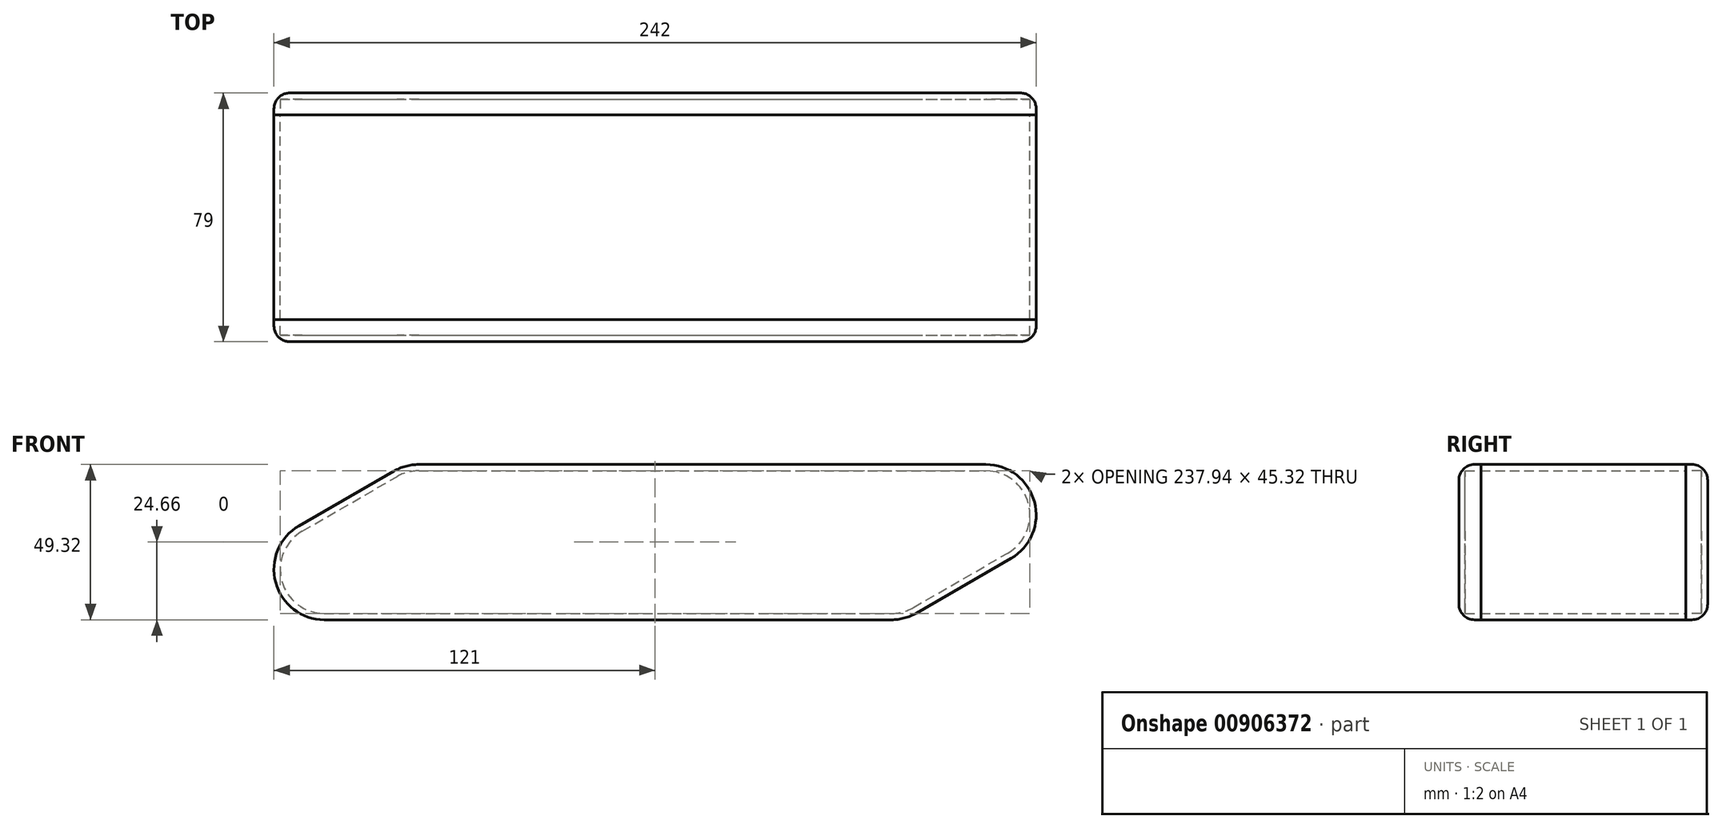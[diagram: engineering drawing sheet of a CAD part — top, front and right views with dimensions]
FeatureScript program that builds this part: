
annotation { "Feature Type Name" : "Feature", "Feature Type Description" : "" }
export const myFeature = defineFeature(function(context is Context, id is Id, definition is map)
    precondition{}
    {
        {
            var Q0;
            Q0=qCreatedBy(makeId("Front.planeOp"),FACE);
            var sketch = newSketch(context, id + "F0", { "sketchPlane" : qUnion([Q0])});
            skCircle(sketch, "E0", {"center": v(0, 0) * mm, "radius": 9 * mm});
            skCircle(sketch, "E1.1.0.0", {"center": v(20, 0) * mm, "radius": 9 * mm});
            skCircle(sketch, "E1.2.0.0", {"center": v(40, 0) * mm, "radius": 9 * mm});
            skCircle(sketch, "E1.3.0.0", {"center": v(60, 0) * mm, "radius": 9 * mm});
            skCircle(sketch, "E1.4.0.0", {"center": v(80, 0) * mm, "radius": 9 * mm});
            skCircle(sketch, "E1.5.0.0", {"center": v(100, 0) * mm, "radius": 9 * mm});
            skCircle(sketch, "E1.6.0.0", {"center": v(120, 0) * mm, "radius": 9 * mm});
            skCircle(sketch, "E1.7.0.0", {"center": v(140, 0) * mm, "radius": 9 * mm});
            skCircle(sketch, "E1.8.0.0", {"center": v(160, 0) * mm, "radius": 9 * mm});
            skCircle(sketch, "E1.9.0.0", {"center": v(180, 0) * mm, "radius": 9 * mm});
            skLineSegment(sketch, "E1.direction1", {"start": v(0, 0) * mm, "end": v(20, 0) * mm, "construction": true});
            skCircle(sketch, "E2", {"center": v(30, 17.32) * mm, "radius": 9 * mm});
            skCircle(sketch, "E3.1.0.0", {"center": v(50, 17.32) * mm, "radius": 9 * mm});
            skCircle(sketch, "E3.2.0.0", {"center": v(70, 17.32) * mm, "radius": 9 * mm});
            skCircle(sketch, "E3.3.0.0", {"center": v(90, 17.32) * mm, "radius": 9 * mm});
            skCircle(sketch, "E3.4.0.0", {"center": v(110, 17.32) * mm, "radius": 9 * mm});
            skCircle(sketch, "E3.5.0.0", {"center": v(130, 17.32) * mm, "radius": 9 * mm});
            skCircle(sketch, "E3.6.0.0", {"center": v(150, 17.32) * mm, "radius": 9 * mm});
            skCircle(sketch, "E3.7.0.0", {"center": v(170, 17.32) * mm, "radius": 9 * mm});
            skCircle(sketch, "E3.8.0.0", {"center": v(190, 17.32) * mm, "radius": 9 * mm});
            skCircle(sketch, "E3.9.0.0", {"center": v(210, 17.32) * mm, "radius": 9 * mm});
            skLineSegment(sketch, "E3.direction1", {"start": v(30, 17.32) * mm, "end": v(50, 17.32) * mm, "construction": true});
            skSolve(sketch);
        }
        {
            var Q0;
            Q0=qCreatedBy(makeId("Front.planeOp"),FACE);
            var sketch = newSketch(context, id + "F1", { "sketchPlane" : qUnion([Q0])});
            skArc(sketch, "E4.0", {"start": v(-4.5, 7.8) * mm, "mid": v(-8.7, -2.33) * mm, "end": v(0, -9) * mm});
            skArc(sketch, "E5.0", {"start": v(30, 26.32) * mm, "mid": v(27.67, 26.01) * mm, "end": v(25.5, 25.11) * mm});
            skArc(sketch, "E6.0", {"start": v(214.5, 9.53) * mm, "mid": v(218.7, 19.65) * mm, "end": v(210, 26.32) * mm});
            skArc(sketch, "E7.0", {"start": v(180, -9) * mm, "mid": v(182.33, -8.7) * mm, "end": v(184.5, -7.8) * mm});
            skLineSegment(sketch, "E8", {"start": v(-4.5, 7.8) * mm, "end": v(25.5, 25.11) * mm});
            skLineSegment(sketch, "E9", {"start": v(0, -9) * mm, "end": v(180, -9) * mm});
            skLineSegment(sketch, "E10", {"start": v(184.5, -7.8) * mm, "end": v(214.5, 9.53) * mm});
            skLineSegment(sketch, "E11", {"start": v(30, 26.32) * mm, "end": v(210, 26.32) * mm});
            skArc(sketch, "E12.0", {"start": v(30, 31.32) * mm, "mid": v(26.38, 30.84) * mm, "end": v(23, 29.44) * mm});
            skLineSegment(sketch, "E12.1", {"start": v(-7, 12.12) * mm, "end": v(23, 29.44) * mm});
            skLineSegment(sketch, "E12.2", {"start": v(30, 31.32) * mm, "end": v(210, 31.32) * mm});
            skArc(sketch, "E12.3", {"start": v(-7, 12.12) * mm, "mid": v(-13.52, -3.62) * mm, "end": v(0, -14) * mm});
            skArc(sketch, "E12.4", {"start": v(217, 5.2) * mm, "mid": v(223.52, 20.94) * mm, "end": v(210, 31.32) * mm});
            skLineSegment(sketch, "E12.5", {"start": v(187, -12.12) * mm, "end": v(217, 5.2) * mm});
            skArc(sketch, "E12.6", {"start": v(180, -14) * mm, "mid": v(183.62, -13.52) * mm, "end": v(187, -12.12) * mm});
            skLineSegment(sketch, "E12.7", {"start": v(0, -14) * mm, "end": v(180, -14) * mm});
            skArc(sketch, "E13.0", {"start": v(30, 33.32) * mm, "mid": v(25.86, 32.78) * mm, "end": v(22, 31.18) * mm});
            skLineSegment(sketch, "E13.1", {"start": v(-8, 13.86) * mm, "end": v(22, 31.18) * mm});
            skLineSegment(sketch, "E13.2", {"start": v(30, 33.32) * mm, "end": v(210, 33.32) * mm});
            skArc(sketch, "E13.3", {"start": v(-8, 13.86) * mm, "mid": v(-15.45, -4.14) * mm, "end": v(0, -16) * mm});
            skArc(sketch, "E13.4", {"start": v(218, 3.46) * mm, "mid": v(225.45, 21.46) * mm, "end": v(210, 33.32) * mm});
            skLineSegment(sketch, "E13.5", {"start": v(188, -13.86) * mm, "end": v(218, 3.46) * mm});
            skArc(sketch, "E13.6", {"start": v(180, -16) * mm, "mid": v(184.14, -15.45) * mm, "end": v(188, -13.86) * mm});
            skLineSegment(sketch, "E13.7", {"start": v(0, -16) * mm, "end": v(180, -16) * mm});
            skSolve(sketch);
        }
        {
            var Q0;
            Q0=makeQuery(id+"F1.imprint","IMPRINT",FACE,{"disambiguationData":[TD([[makeQuery(id+"F1.imprint","IMPRINT",EDGE,{"derivedFrom":sQuery(id+"F1.wireOp",EDGE,"E12.0")}),-1.0]])]});
            extrude(context, id + "F2", {"entities" : qUnion([Q0]), "depth" : 65 * mm, "offsetDistance" : 25 * mm});
        }
        {
            var Q0;
            Q0=makeQuery(id+"F2.opExtrude","CAP_FACE",FACE,{"disambiguationData":[OSD([sQuery(id+"F1.wireOp",EDGE,"E12.0"),sQuery(id+"F1.wireOp",EDGE,"E12.1"),sQuery(id+"F1.wireOp",EDGE,"E12.2"),sQuery(id+"F1.wireOp",EDGE,"E12.3"),sQuery(id+"F1.wireOp",EDGE,"E12.4"),sQuery(id+"F1.wireOp",EDGE,"E12.5"),sQuery(id+"F1.wireOp",EDGE,"E12.6"),sQuery(id+"F1.wireOp",EDGE,"E12.7"),sQuery(id+"F1.wireOp",EDGE,"E13.0"),sQuery(id+"F1.wireOp",EDGE,"E13.1"),sQuery(id+"F1.wireOp",EDGE,"E13.2"),sQuery(id+"F1.wireOp",EDGE,"E13.3"),sQuery(id+"F1.wireOp",EDGE,"E13.4"),sQuery(id+"F1.wireOp",EDGE,"E13.5"),sQuery(id+"F1.wireOp",EDGE,"E13.6"),sQuery(id+"F1.wireOp",EDGE,"E13.7")])],"isStart":false});
            var sketch = newSketch(context, id + "F3", { "sketchPlane" : qUnion([Q0])});
            skArc(sketch, "E14.0.0", {"start": v(-8, 13.86) * mm, "mid": v(-15.45, -4.14) * mm, "end": v(0, -16) * mm});
            skLineSegment(sketch, "E14.0.1", {"start": v(0, -16) * mm, "end": v(180, -16) * mm});
            skArc(sketch, "E14.0.2", {"start": v(180, -16) * mm, "mid": v(184.14, -15.45) * mm, "end": v(188, -13.86) * mm});
            skLineSegment(sketch, "E14.0.3", {"start": v(188, -13.86) * mm, "end": v(218, 3.46) * mm});
            skArc(sketch, "E14.0.4", {"start": v(218, 3.46) * mm, "mid": v(225.45, 21.46) * mm, "end": v(210, 33.32) * mm});
            skLineSegment(sketch, "E14.0.5", {"start": v(210, 33.32) * mm, "end": v(30, 33.32) * mm});
            skArc(sketch, "E14.0.6", {"start": v(30, 33.32) * mm, "mid": v(25.86, 32.78) * mm, "end": v(22, 31.18) * mm});
            skLineSegment(sketch, "E14.0.7", {"start": v(22, 31.18) * mm, "end": v(-8, 13.86) * mm});
            skLineSegment(sketch, "E15.0", {"start": v(30, 31.32) * mm, "end": v(210, 31.32) * mm});
            skArc(sketch, "E16.0", {"start": v(30, 31.32) * mm, "mid": v(26.38, 30.84) * mm, "end": v(23, 29.44) * mm});
            skLineSegment(sketch, "E17.0", {"start": v(-7, 12.12) * mm, "end": v(23, 29.44) * mm});
            skArc(sketch, "E18.0", {"start": v(-7, 12.12) * mm, "mid": v(-13.52, -3.62) * mm, "end": v(0, -14) * mm});
            skLineSegment(sketch, "E19.0", {"start": v(0, -14) * mm, "end": v(180, -14) * mm});
            skArc(sketch, "E20.0", {"start": v(180, -14) * mm, "mid": v(183.62, -13.52) * mm, "end": v(187, -12.12) * mm});
            skLineSegment(sketch, "E21.0", {"start": v(187, -12.12) * mm, "end": v(217, 5.2) * mm});
            skArc(sketch, "E22.0", {"start": v(217, 5.2) * mm, "mid": v(223.52, 20.94) * mm, "end": v(210, 31.32) * mm});
            skSolve(sketch);
        }
        {
            var Q0;
            Q0=makeQuery(id+"F3.imprint","IMPRINT",FACE,{"disambiguationData":[TD([[makeQuery(id+"F3.imprint","IMPRINT",EDGE,{"derivedFrom":sQuery(id+"F3.wireOp",EDGE,"E14.0.0")}),1.0]])]});
            extrude(context, id + "F4", {"entities" : qUnion([Q0]), "depth" : 5 * mm, "offsetDistance" : 25 * mm});
        }
        {
            var Q0;
            Q0=makeQuery(id+"F4.opExtrude","CAP_FACE",FACE,{"disambiguationData":[OSD([sQuery(id+"F3.wireOp",EDGE,"E14.0.0"),sQuery(id+"F3.wireOp",EDGE,"E14.0.1"),sQuery(id+"F3.wireOp",EDGE,"E14.0.2"),sQuery(id+"F3.wireOp",EDGE,"E14.0.3"),sQuery(id+"F3.wireOp",EDGE,"E14.0.4"),sQuery(id+"F3.wireOp",EDGE,"E14.0.5"),sQuery(id+"F3.wireOp",EDGE,"E14.0.6"),sQuery(id+"F3.wireOp",EDGE,"E14.0.7"),sQuery(id+"F3.wireOp",EDGE,"E15.0"),sQuery(id+"F3.wireOp",EDGE,"E16.0"),sQuery(id+"F3.wireOp",EDGE,"E17.0"),sQuery(id+"F3.wireOp",EDGE,"E18.0"),sQuery(id+"F3.wireOp",EDGE,"E19.0"),sQuery(id+"F3.wireOp",EDGE,"E20.0"),sQuery(id+"F3.wireOp",EDGE,"E21.0"),sQuery(id+"F3.wireOp",EDGE,"E22.0")])],"isStart":false});
            var sketch = newSketch(context, id + "F5", { "sketchPlane" : qUnion([Q0])});
            skLineSegment(sketch, "E23.0.0", {"start": v(22, 31.18) * mm, "end": v(-8, 13.86) * mm});
            skArc(sketch, "E23.0.1", {"start": v(-8, 13.86) * mm, "mid": v(-15.45, -4.14) * mm, "end": v(0, -16) * mm});
            skLineSegment(sketch, "E23.0.2", {"start": v(0, -16) * mm, "end": v(180, -16) * mm});
            skArc(sketch, "E23.0.3", {"start": v(180, -16) * mm, "mid": v(184.14, -15.45) * mm, "end": v(188, -13.86) * mm});
            skLineSegment(sketch, "E23.0.4", {"start": v(188, -13.86) * mm, "end": v(218, 3.46) * mm});
            skArc(sketch, "E23.0.5", {"start": v(218, 3.46) * mm, "mid": v(225.45, 21.46) * mm, "end": v(210, 33.32) * mm});
            skLineSegment(sketch, "E23.0.6", {"start": v(210, 33.32) * mm, "end": v(30, 33.32) * mm});
            skArc(sketch, "E23.0.7", {"start": v(30, 33.32) * mm, "mid": v(25.86, 32.78) * mm, "end": v(22, 31.18) * mm});
            skSolve(sketch);
        }
        {
            var Q0;
            Q0=makeQuery(id+"F5.imprint","IMPRINT",FACE,{"disambiguationData":[TD([[makeQuery(id+"F5.imprint","IMPRINT",EDGE,{"derivedFrom":makeQuery(id+"F4.opExtrude","CAP_EDGE",EDGE,{"disambiguationData":[OSD([sQuery(id+"F3.wireOp",EDGE,"E15.0")])],"isStart":false})}),-1.0]])]});
            var Q1;
            Q1=makeQuery(id+"F5.imprint","IMPRINT",FACE,{"disambiguationData":[TD([[makeQuery(id+"F5.imprint","IMPRINT",EDGE,{"derivedFrom":sQuery(id+"F5.wireOp",EDGE,"E23.0.0")}),-1.0]])]});
            extrude(context, id + "F6", {"entities" : qUnion([Q0, Q1]), "operationType" : NewBodyOperationType.ADD, "depth" : 2 * mm, "offsetDistance" : 25 * mm});
        }
        {
            var Q0;
            Q0=makeQuery(id+"F6.opExtrude","CAP_FACE",FACE,{"disambiguationData":[OSD([sQuery(id+"F5.wireOp",EDGE,"E23.0.0"),sQuery(id+"F5.wireOp",EDGE,"E23.0.1"),sQuery(id+"F5.wireOp",EDGE,"E23.0.2"),sQuery(id+"F5.wireOp",EDGE,"E23.0.3"),sQuery(id+"F5.wireOp",EDGE,"E23.0.4"),sQuery(id+"F5.wireOp",EDGE,"E23.0.5"),sQuery(id+"F5.wireOp",EDGE,"E23.0.6"),sQuery(id+"F5.wireOp",EDGE,"E23.0.7")])],"isStart":false});
            fillet(context, id + "F7", {"entities" : qUnion([Q0]), "radius" : 5 * mm, "tangentPropagation" : true, "allowEdgeOverflow" : false});
        }
        {
            var Q0;
            Q0=qCreatedBy(makeId("Front.planeOp"),FACE);
            cPlane(context, id + "F8", {"entities" : qUnion([Q0]), "cplaneType" : CPlaneType.OFFSET, "offset" : 32.5 * mm, "width" : 150 * mm, "height" : 150 * mm});
        }
        {
            var Q0;
            Q0=makeQuery(id+"F4.opExtrude","SWEPT_BODY",BODY,{"disambiguationData":[OSD([sQuery(id+"F3.wireOp",EDGE,"E14.0.0"),sQuery(id+"F3.wireOp",EDGE,"E14.0.1"),sQuery(id+"F3.wireOp",EDGE,"E14.0.2"),sQuery(id+"F3.wireOp",EDGE,"E14.0.3"),sQuery(id+"F3.wireOp",EDGE,"E14.0.4"),sQuery(id+"F3.wireOp",EDGE,"E14.0.5"),sQuery(id+"F3.wireOp",EDGE,"E14.0.6"),sQuery(id+"F3.wireOp",EDGE,"E14.0.7"),sQuery(id+"F3.wireOp",EDGE,"E15.0"),sQuery(id+"F3.wireOp",EDGE,"E16.0"),sQuery(id+"F3.wireOp",EDGE,"E17.0"),sQuery(id+"F3.wireOp",EDGE,"E18.0"),sQuery(id+"F3.wireOp",EDGE,"E19.0"),sQuery(id+"F3.wireOp",EDGE,"E20.0"),sQuery(id+"F3.wireOp",EDGE,"E21.0"),sQuery(id+"F3.wireOp",EDGE,"E22.0")])]});
            var Q1;
            Q1=qCreatedBy(id+"F8.planeOp",FACE);
            mirror(context, id + "F9", {"entities" : qUnion([Q0]), "mirrorPlane" : qUnion([Q1])});
        }
    });
